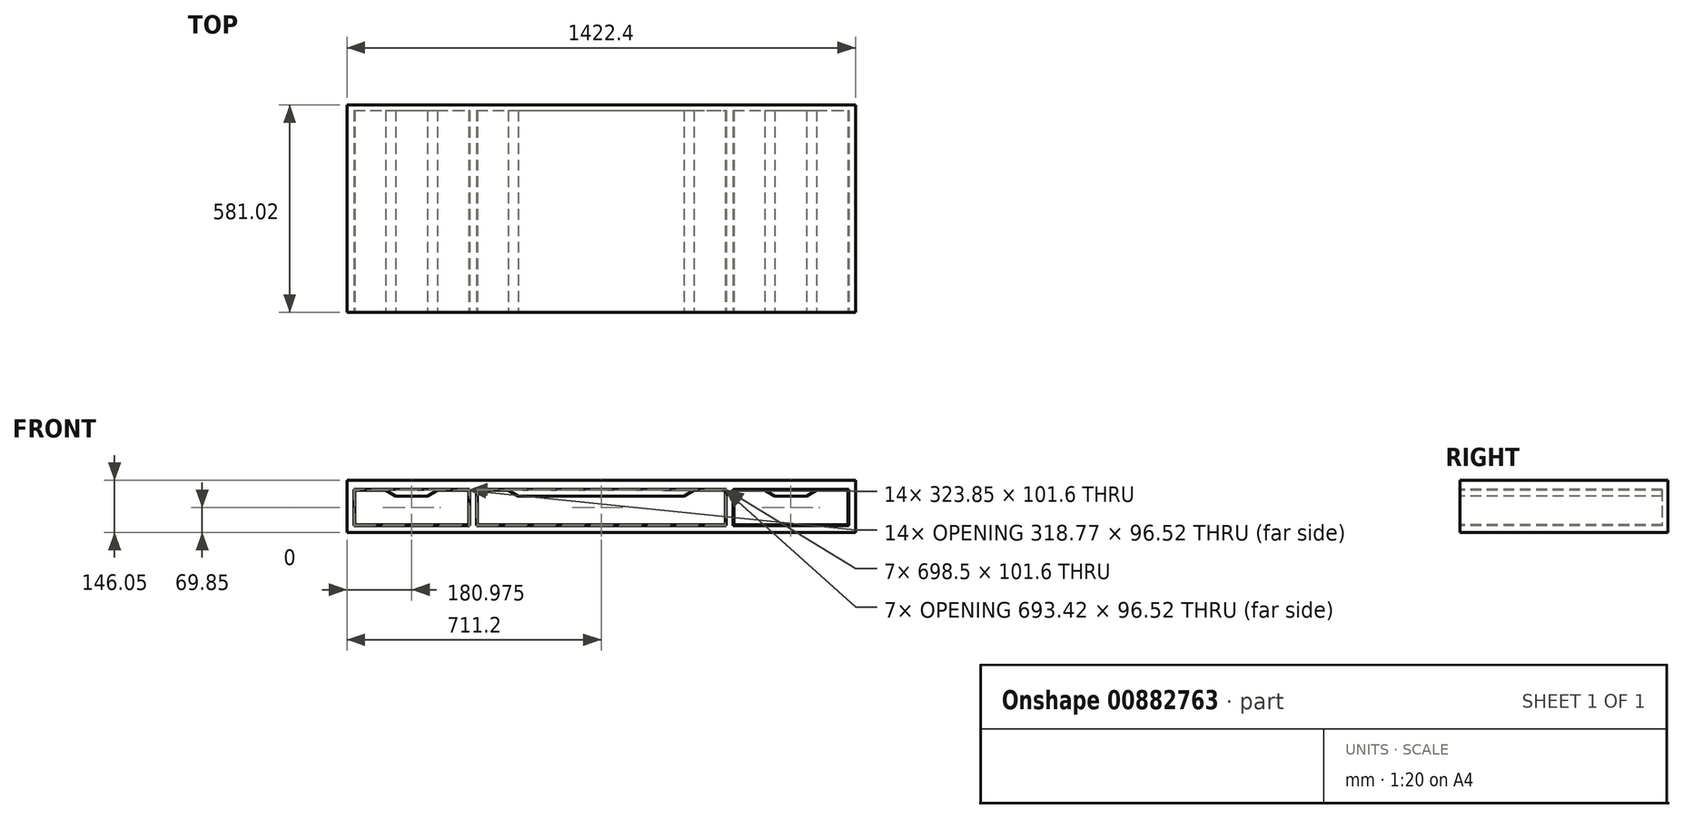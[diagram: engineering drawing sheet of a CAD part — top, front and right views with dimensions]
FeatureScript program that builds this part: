
annotation { "Feature Type Name" : "Feature", "Feature Type Description" : "" }
export const myFeature = defineFeature(function(context is Context, id is Id, definition is map)
    precondition{}
    {
        {
            var Q0;
            Q0=qCreatedBy(makeId("Front.planeOp"),FACE);
            var sketch = newSketch(context, id + "F0", { "sketchPlane" : qUnion([Q0])});
            skLineSegment(sketch, "E0.bottom", {"start": v(0, 0) * mm, "end": v(1422.4, 0) * mm});
            skLineSegment(sketch, "E0.top", {"start": v(0, 146.05) * mm, "end": v(1422.4, 146.05) * mm});
            skLineSegment(sketch, "E0.left", {"start": v(0, 0) * mm, "end": v(0, 146.05) * mm});
            skLineSegment(sketch, "E0.right", {"start": v(1422.4, 0) * mm, "end": v(1422.4, 146.05) * mm});
            skSolve(sketch);
        }
        {
            var Q0;
            Q0=makeQuery(id+"F0.imprint","IMPRINT",FACE,{"disambiguationData":[TD([[makeQuery(id+"F0.imprint","IMPRINT",EDGE,{"derivedFrom":sQuery(id+"F0.wireOp",EDGE,"E0.bottom")}),1.0]])]});
            extrude(context, id + "F1", {"entities" : qUnion([Q0]), "depth" : 581.02 * mm, "offsetDistance" : 25.4 * mm});
        }
        {
            var Q0;
            Q0=makeQuery(id+"F1.opExtrude","CAP_FACE",FACE,{"disambiguationData":[OSD([sQuery(id+"F0.wireOp",EDGE,"E0.bottom"),sQuery(id+"F0.wireOp",EDGE,"E0.top"),sQuery(id+"F0.wireOp",EDGE,"E0.left"),sQuery(id+"F0.wireOp",EDGE,"E0.right")])],"isStart":false});
            var sketch = newSketch(context, id + "F2", { "sketchPlane" : qUnion([Q0])});
            skLineSegment(sketch, "E1.bottom", {"start": v(19.05, 120.65) * mm, "end": v(342.9, 120.65) * mm});
            skLineSegment(sketch, "E1.top", {"start": v(19.05, 19.05) * mm, "end": v(342.9, 19.05) * mm});
            skLineSegment(sketch, "E1.left", {"start": v(19.05, 120.65) * mm, "end": v(19.05, 19.05) * mm});
            skLineSegment(sketch, "E1.right", {"start": v(342.9, 120.65) * mm, "end": v(342.9, 19.05) * mm});
            skLineSegment(sketch, "E2.bottom", {"start": v(361.95, 19.05) * mm, "end": v(1060.45, 19.05) * mm});
            skLineSegment(sketch, "E2.top", {"start": v(361.95, 120.65) * mm, "end": v(1060.45, 120.65) * mm});
            skLineSegment(sketch, "E2.left", {"start": v(361.95, 19.05) * mm, "end": v(361.95, 120.65) * mm});
            skLineSegment(sketch, "E2.right", {"start": v(1060.45, 19.05) * mm, "end": v(1060.45, 120.65) * mm});
            skLineSegment(sketch, "E3.bottom", {"start": v(1079.5, 120.65) * mm, "end": v(1403.35, 120.65) * mm});
            skLineSegment(sketch, "E3.top", {"start": v(1079.5, 19.05) * mm, "end": v(1403.35, 19.05) * mm});
            skLineSegment(sketch, "E3.left", {"start": v(1079.5, 120.65) * mm, "end": v(1079.5, 19.05) * mm});
            skLineSegment(sketch, "E3.right", {"start": v(1403.35, 120.65) * mm, "end": v(1403.35, 19.05) * mm});
            skLineSegment(sketch, "E4", {"start": v(104.77, 120.65) * mm, "end": v(136.53, 101.6) * mm});
            skLineSegment(sketch, "E5", {"start": v(136.53, 101.6) * mm, "end": v(225.43, 101.6) * mm});
            skLineSegment(sketch, "E6", {"start": v(225.42, 101.6) * mm, "end": v(257.18, 120.65) * mm});
            skLineSegment(sketch, "E7", {"start": v(1165.23, 120.65) * mm, "end": v(1196.98, 101.6) * mm});
            skLineSegment(sketch, "E8", {"start": v(1196.98, 101.6) * mm, "end": v(1285.88, 101.6) * mm});
            skLineSegment(sketch, "E9", {"start": v(1285.88, 101.6) * mm, "end": v(1317.63, 120.65) * mm});
            skLineSegment(sketch, "E10", {"start": v(447.68, 120.65) * mm, "end": v(479.43, 101.6) * mm});
            skLineSegment(sketch, "E11", {"start": v(479.43, 101.6) * mm, "end": v(942.98, 101.6) * mm});
            skLineSegment(sketch, "E12", {"start": v(942.98, 101.6) * mm, "end": v(974.73, 120.65) * mm});
            skLineSegment(sketch, "E13.bottom", {"start": v(21.59, 118.1) * mm, "end": v(340.36, 118.11) * mm});
            skLineSegment(sketch, "E13.top", {"start": v(21.6, 21.59) * mm, "end": v(340.36, 21.6) * mm});
            skLineSegment(sketch, "E13.left", {"start": v(21.59, 118.1) * mm, "end": v(21.6, 21.59) * mm});
            skLineSegment(sketch, "E13.right", {"start": v(340.36, 118.11) * mm, "end": v(340.36, 21.6) * mm});
            skLineSegment(sketch, "E14.bottom", {"start": v(364.5, 118.11) * mm, "end": v(1057.9, 118.11) * mm});
            skLineSegment(sketch, "E14.top", {"start": v(364.5, 21.6) * mm, "end": v(1057.9, 21.6) * mm});
            skLineSegment(sketch, "E14.left", {"start": v(364.5, 118.11) * mm, "end": v(364.5, 21.6) * mm});
            skLineSegment(sketch, "E14.right", {"start": v(1057.9, 118.11) * mm, "end": v(1057.9, 21.6) * mm});
            skLineSegment(sketch, "E15.bottom", {"start": v(1082.04, 118.11) * mm, "end": v(1400.81, 118.11) * mm});
            skLineSegment(sketch, "E15.top", {"start": v(1082.04, 21.6) * mm, "end": v(1400.81, 21.6) * mm});
            skLineSegment(sketch, "E15.left", {"start": v(1082.04, 118.11) * mm, "end": v(1082.04, 21.6) * mm});
            skLineSegment(sketch, "E15.right", {"start": v(1400.81, 118.11) * mm, "end": v(1400.81, 21.6) * mm});
            skSolve(sketch);
        }
        {
            var Q0;
            Q0=makeQuery(id+"F2.imprint","IMPRINT",FACE,{"disambiguationData":[TD([[makeQuery(id+"F2.imprint","IMPRINT",EDGE,{"derivedFrom":sQuery(id+"F2.wireOp",EDGE,"E1.top")}),1.0]])]});
            var Q1;
            Q1=makeQuery(id+"F2.imprint","IMPRINT",FACE,{"disambiguationData":[TD([[makeQuery(id+"F2.imprint","IMPRINT",EDGE,{"derivedFrom":sQuery(id+"F2.wireOp",EDGE,"E2.bottom")}),1.0]])]});
            var Q2;
            Q2=makeQuery(id+"F2.imprint","IMPRINT",FACE,{"disambiguationData":[TD([[makeQuery(id+"F2.imprint","IMPRINT",EDGE,{"derivedFrom":sQuery(id+"F2.wireOp",EDGE,"E3.top")}),1.0]])]});
            var Q3;
            {var subQ0=sQuery(id+"F2.wireOp",EDGE,"E7");var subQ1=sQuery(id+"F2.wireOp",EDGE,"E3.bottom");var subQ2=makeQuery(id+"F2.imprint","INTERSECT",VERTEX,{"derivedFrom":[subQ1,subQ0]});Q3=makeQuery(id+"F2.imprint","IMPRINT",FACE,{"disambiguationData":[TD([[makeQuery(id+"F2.imprint","IMPRINT",EDGE,{"disambiguationData":[TD([[subQ2,-1.0]])],"derivedFrom":subQ1}),-1.0]])]});}
            var Q4;
            {var subQ0=sQuery(id+"F2.wireOp",EDGE,"E8");Q4=makeQuery(id+"F2.imprint","IMPRINT",FACE,{"disambiguationData":[TD([[makeQuery(id+"F2.imprint","IMPRINT",EDGE,{"derivedFrom":subQ0}),1.0]])]});}
            var Q5;
            {var subQ0=sQuery(id+"F2.wireOp",EDGE,"E11");Q5=makeQuery(id+"F2.imprint","IMPRINT",FACE,{"disambiguationData":[TD([[makeQuery(id+"F2.imprint","IMPRINT",EDGE,{"derivedFrom":subQ0}),1.0]])]});}
            var Q6;
            {var subQ0=sQuery(id+"F2.wireOp",EDGE,"E10");var subQ1=sQuery(id+"F2.wireOp",EDGE,"E2.top");var subQ2=makeQuery(id+"F2.imprint","INTERSECT",VERTEX,{"derivedFrom":[subQ1,subQ0]});Q6=makeQuery(id+"F2.imprint","IMPRINT",FACE,{"disambiguationData":[TD([[makeQuery(id+"F2.imprint","IMPRINT",EDGE,{"disambiguationData":[TD([[subQ2,-1.0]])],"derivedFrom":subQ1}),-1.0]])]});}
            var Q7;
            {var subQ0=sQuery(id+"F2.wireOp",EDGE,"E4");var subQ1=sQuery(id+"F2.wireOp",EDGE,"E1.bottom");var subQ2=makeQuery(id+"F2.imprint","INTERSECT",VERTEX,{"derivedFrom":[subQ1,subQ0]});Q7=makeQuery(id+"F2.imprint","IMPRINT",FACE,{"disambiguationData":[TD([[makeQuery(id+"F2.imprint","IMPRINT",EDGE,{"disambiguationData":[TD([[subQ2,-1.0]])],"derivedFrom":subQ1}),-1.0]])]});}
            var Q8;
            {var subQ0=sQuery(id+"F2.wireOp",EDGE,"E5");Q8=makeQuery(id+"F2.imprint","IMPRINT",FACE,{"disambiguationData":[TD([[makeQuery(id+"F2.imprint","IMPRINT",EDGE,{"derivedFrom":subQ0}),1.0]])]});}
            extrude(context, id + "F3", {"entities" : qUnion([Q0, Q1, Q2, Q3, Q4, Q5, Q6, Q7, Q8]), "operationType" : NewBodyOperationType.REMOVE, "oppositeDirection" : true, "depth" : 565.15 * mm, "offsetDistance" : 25.4 * mm});
        }
    });
